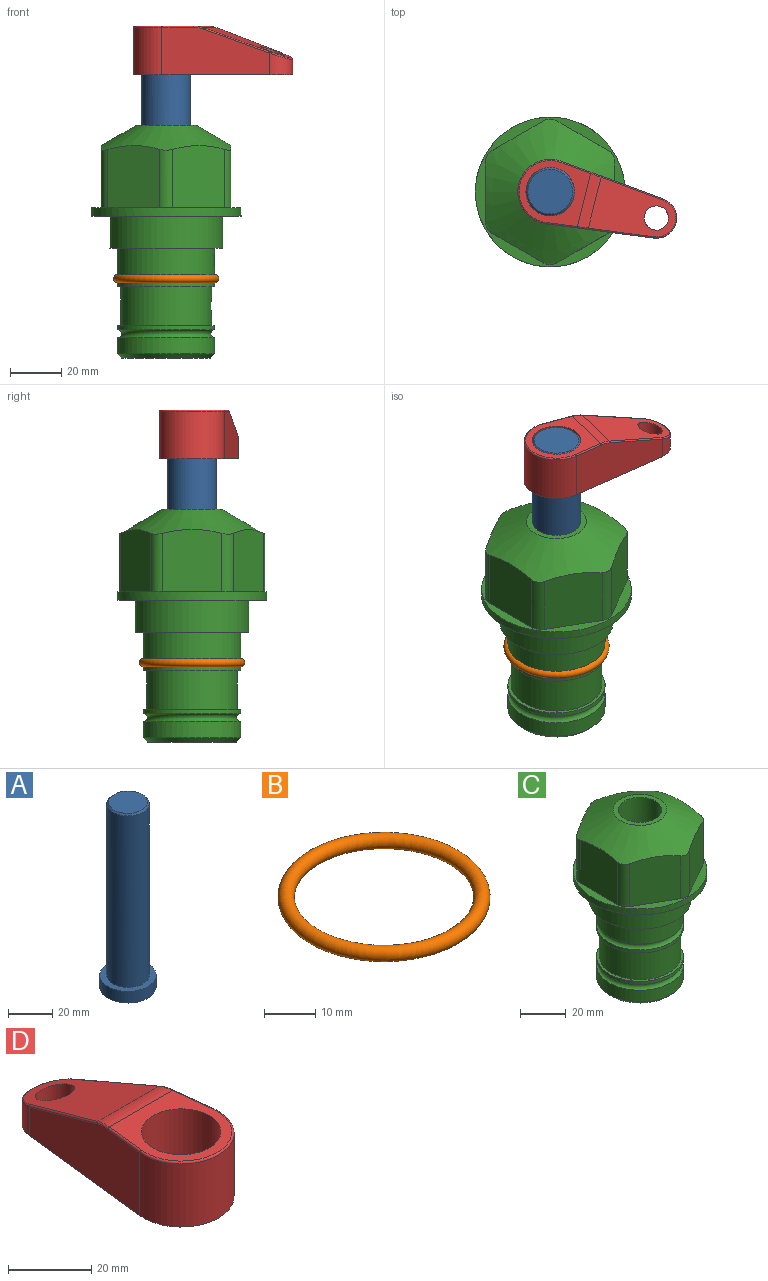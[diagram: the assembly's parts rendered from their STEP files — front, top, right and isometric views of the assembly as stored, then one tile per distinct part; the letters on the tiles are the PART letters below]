
ASSEMBLY  parts=4 mates=2
PART A: 6 faces, bbox 25.4x25.4x101.6 mm
  f0: plane 17.46x17.46mm, normal (0,0,1), area 239.5mm2, adj f5
  f1: plane 25.4x25.4mm, normal (0,0,-1), area 506.7mm2, adj f2
  f2: cylinder r=12.7mm len=25.4mm, axis (0,0,1), area 506.7mm2, adj f1,f3
  f3: plane 25.4x25.4mm, normal (0,0,1), area 221.7mm2, adj f2,f4
  f4: cylinder r=9.53mm len=94.46mm, axis (0,0,1), area 5653mm2, adj f3,f5
  f5: cone r=8.73mm half-angle=45deg, axis (0,0,-1), area 64.4mm2, adj f0,f4
PART B: 1 faces, bbox 44.7x44.7x3.2 mm
  f0: torus R=19.05mm, axis (0,0,1), area 1193.9mm2
PART C: 36 faces, bbox 58.7x58.7x91.2 mm
  f0: cylinder r=17.78mm len=35.56mm, axis (0,0,1), area 1670.8mm2, adj f23,f24,f31
  f1: cylinder r=19.05mm len=38.1mm, axis (0,0,1), area 1191.9mm2, adj f26,f27,f30
  f2: plane 58.66x58.66mm, normal (0,0,-1), area 1150.6mm2, adj f3,f28
  f3: cylinder r=29.33mm len=58.66mm, axis (0,0,-1), area 585.1mm2, adj f2,f4
  f4: plane 58.66x58.66mm, normal (0,0,1), area 475.9mm2, adj f3,f5,f6,f7,f8,f9,f10,f11
  f5: plane 24.5x20.32mm, normal (-0.5,0.87,0), area 562.8mm2, adj f4,f15,f16,f17
  f6: plane 24.5x20.32mm, normal (0.5,0.87,0), area 562.8mm2, adj f4,f14,f15,f17
  f7: plane 24.5x23.48mm, normal (1,0,0), area 562.8mm2, adj f4,f13,f14,f17
  f8: plane 24.5x20.32mm, normal (0.5,-0.87,0), area 562.8mm2, adj f4,f12,f13,f17
  f9: plane 24.5x20.32mm, normal (-0.5,-0.87,0), area 562.8mm2, adj f4,f11,f12,f17
  f10: plane 24.5x23.48mm, normal (-1,0,0), area 562.8mm2, adj f4,f11,f16,f17
  f11: cylinder r=5.08mm len=23.01mm, axis (0,0,-1), area 121.2mm2, adj f4,f9,f10,f17
  f12: cylinder r=5.08mm len=23.01mm, axis (0,0,-1), area 121.2mm2, adj f4,f8,f9,f17
  f13: cylinder r=5.08mm len=23.01mm, axis (0,0,-1), area 121.2mm2, adj f4,f7,f8,f17
  f14: cylinder r=5.08mm len=23.01mm, axis (0,0,-1), area 121.2mm2, adj f4,f6,f7,f17
  f15: cylinder r=5.08mm len=23.01mm, axis (0,0,-1), area 121.2mm2, adj f4,f5,f6,f17
  f16: cylinder r=5.08mm len=23.01mm, axis (0,0,-1), area 121.2mm2, adj f4,f5,f10,f17
  f17: cone r=11.73mm half-angle=60deg, axis (0,0,-1), area 2071.8mm2, adj f5,f6,f7,f8,f9,f10,f11,f12
  f18: plane 23.46x23.46mm, normal (0,0,1), area 147.4mm2, adj f17,f35
  f19: plane 34.93x34.93mm, normal (0,0,-1), area 958mm2, adj f29
  f20: cylinder r=19.05mm len=38.1mm, axis (0,0,1), area 760.1mm2, adj f21,f29
  f21: torus R=19.05mm, axis (0,0,1), area 565.3mm2, adj f20,f22
  f22: cylinder r=19.05mm len=38.1mm, axis (0,0,1), area 190mm2, adj f21,f23
  f23: plane 38.1x38.1mm, normal (0,0,1), area 146.9mm2, adj f0,f22
  f24: plane 38.1x38.1mm, normal (0,0,-1), area 146.9mm2, adj f0,f25
  f25: cylinder r=19.05mm len=38.1mm, axis (0,0,1), area 190mm2, adj f24,f26
  f26: torus R=19.05mm, axis (0,0,1), area 565.3mm2, adj f1,f25
  f27: plane 44.45x44.45mm, normal (0,0,-1), area 411.7mm2, adj f1,f28
  f28: cylinder r=22.23mm len=44.45mm, axis (0,0,1), area 1773.5mm2, adj f2,f27
  f29: cone r=19.05mm half-angle=45deg, axis (0,0,1), area 257.5mm2, adj f19,f20
  f30: cylinder r=3.17mm len=6.75mm, axis (-1,0,0), area 128mm2, adj f1,f33
  f31: cylinder r=3.17mm len=6.35mm, axis (-1,0,0), area 102.5mm2, adj f0,f33
  f32: plane 25.4x25.4mm, normal (0,0,1), area 506.7mm2, adj f33
  f33: cylinder r=12.7mm len=66.42mm, axis (0,0,-1), area 5236.2mm2, adj f30,f31,f32,f34
  f34: cone r=9.53mm half-angle=30deg, axis (0,0,-1), area 443.4mm2, adj f33,f35
  f35: cylinder r=9.53mm len=19.05mm, axis (0,0,-1), area 849mm2, adj f18,f34
PART D: 44 faces, bbox 27.5x64.5x19.1 mm
  f0: plane 2.3x0.95mm, normal (0,0,-1), area 1mm2, adj f25,f30,f34
  f1: plane 63.5x25.4mm, normal (0,0,-1), area 561.7mm2, adj f2,f3,f4,f5,f6,f7,f19,f20
  f2: cylinder r=12.7mm len=25.4mm, axis (0,0,-1), area 792.2mm2, adj f1,f3,f5,f13
  f3: plane 42.33x18.54mm, normal (0.99,0.11,0), area 647mm2, adj f1,f2,f4,f11,f12,f14
  f4: cylinder r=7.94mm len=15.78mm, axis (0,0,-1), area 158.6mm2, adj f1,f3,f5,f16
  f5: plane 42.33x18.54mm, normal (-0.99,0.11,0), area 647mm2, adj f1,f2,f4,f15,f17,f18
  f6: cylinder r=9.53mm len=19.05mm, axis (0,0,-1), area 1140.1mm2, adj f1,f8
  f7: cylinder r=4.76mm len=10.98mm, axis (0,0,-1), area 276.1mm2, adj f1,f9
  f8: plane 25.83x24.38mm, normal (0,0,1), area 262.2mm2, adj f6,f10,f11,f13,f15
  f9: plane 32.49x20.55mm, normal (0,0.34,0.94), area 489.9mm2, adj f7,f10,f14,f16,f18
  f10: cylinder r=12.7mm len=21.49mm, axis (-1,0,0), area 93.2mm2, adj f8,f9,f12,f17
  f11: cylinder r=0.51mm len=12.34mm, axis (0.11,-0.99,0), area 9.9mm2, adj f3,f8,f12,f13
  f12: bspline ~7.62x1.64mm, area 3.5mm2, adj f3,f10,f11,f14
  f13: torus R=12.19mm, axis (0,0,1), area 33.6mm2, adj f2,f8,f11,f15
  f14: cylinder r=0.51mm len=26.01mm, axis (0.1,-0.93,0.34), area 21.6mm2, adj f3,f9,f12,f16
  f15: cylinder r=0.51mm len=12.34mm, axis (0.11,0.99,0), area 9.9mm2, adj f5,f8,f13,f17
  f16: bspline ~15.78x7.05mm, area 15.7mm2, adj f4,f9,f14,f18
  f17: bspline ~7.62x1.64mm, area 3.5mm2, adj f5,f10,f15,f18
  f18: cylinder r=0.51mm len=26.01mm, axis (0.1,0.93,-0.34), area 21.6mm2, adj f5,f9,f16,f17
  f19: plane 21.6x14.29mm, normal (-0.99,-0.11,0), area 242.6mm2, adj f1,f26,f28,f34,f36,f38
  f20: plane 21.6x14.29mm, normal (0.99,-0.11,0), area 242.6mm2, adj f1,f27,f29,f37,f39,f41
  f21: cylinder r=12.7mm len=14.29mm, axis (0,0,-1), area 173.2mm2, adj f1,f26,f27,f30,f31,f33
  f22: cylinder r=7.94mm len=7.63mm, axis (0,0,-1), area 53.8mm2, adj f1,f28,f29,f42
  f23: plane 2.3x0.95mm, normal (0,0,-1), area 1mm2, adj f25,f33,f37
  f24: plane 17.94x12.32mm, normal (0,-0.34,-0.94), area 191.2mm2, adj f25,f38,f41,f42
  f25: cylinder r=9.53mm len=12.93mm, axis (-1,0,0), area 37.5mm2, adj f0,f23,f24,f31,f36,f39
  f26: cylinder r=1.59mm len=14.29mm, axis (0,0,-1), area 49mm2, adj f1,f19,f21,f32
  f27: cylinder r=1.59mm len=14.29mm, axis (0,0,-1), area 49mm2, adj f1,f20,f21,f35
  f28: cylinder r=1.59mm len=7.28mm, axis (0,0,-1), area 22.1mm2, adj f1,f19,f22,f40
  f29: cylinder r=1.59mm len=7.28mm, axis (0,0,-1), area 22.1mm2, adj f1,f20,f22,f43
  f30: torus R=14.29mm, axis (0,0,1), area 5.8mm2, adj f0,f21,f31,f32
  f31: bspline ~11.06x2.73mm, area 20.8mm2, adj f21,f25,f30,f33
  f32: sphere r=1.59mm, area 5.4mm2, adj f26,f30,f34
  f33: torus R=14.29mm, axis (0,0,1), area 5.8mm2, adj f21,f23,f31,f35
  f34: cylinder r=1.59mm len=1.68mm, axis (-0.11,0.99,0), area 2.4mm2, adj f0,f19,f32,f36
  f35: sphere r=1.59mm, area 5.4mm2, adj f27,f33,f37
  f36: bspline ~5.82x2.33mm, area 7.7mm2, adj f19,f25,f34,f38
  f37: cylinder r=1.59mm len=1.68mm, axis (0.11,0.99,0), area 2.4mm2, adj f20,f23,f35,f39
  f38: cylinder r=1.59mm len=18.33mm, axis (0.1,-0.93,0.34), area 46.7mm2, adj f19,f24,f36,f40
  f39: bspline ~5.82x2.33mm, area 7.7mm2, adj f20,f25,f37,f41
  f40: sphere r=1.59mm, area 3.6mm2, adj f28,f38,f42
  f41: cylinder r=1.59mm len=18.33mm, axis (0.1,0.93,-0.34), area 46.7mm2, adj f20,f24,f39,f43
  f42: bspline ~8.31x1.84mm, area 15.3mm2, adj f22,f24,f40,f43
  f43: sphere r=1.59mm, area 3.6mm2, adj f29,f41,f42
PLACE A rot(axis=(0,0,1),166.1deg) t=(0,0,0.84)mm
PLACE B at identity
PLACE C at identity fixed
PLACE D rot(axis=(0,0,-1),103.9deg) t=(0,0,55.45)mm
MATE fastened D.f2 <-> A.f2  axis (0,0,-1) through (0,0,74.5)mm
MATE cylindrical A.f2 <-> C.f0  axis (0,0,1) through (0,0,26.48)mm
